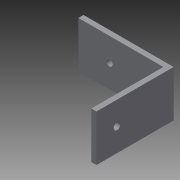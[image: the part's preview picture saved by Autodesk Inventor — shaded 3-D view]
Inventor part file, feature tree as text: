
AUTODESK INVENTOR PART (.ipt)
format: ipt  version: 2015 (Build 190159000, 159)  size: 98,304 bytes
history: native  units: in
note: dims shown in document units (in); Inventor stores cm internally (conversion verified against a paired STEP export)
features: sketch x4, extrude x3, hole x1, projected_geometry x1
ambient origin geometry x8: Origin, YZ Plane, XZ Plane, XY Plane, X Axis, Y Axis, Z Axis, Center Point
bodies: Solid1 (feature_tree)
feature tree (9):
  extrude  "Extrusion1"  Depth=1.75in
  extrude  "Extrusion2"  Depth=0.1in
  hole  "Hole2"  [1 undecoded]
  extrude  "Extrusion3"  Depth=0.05in
  sketch  "Sketch1"  dims[d0=0.9in d1=1.75in]
  sketch  "Sketch2"  dims[d2=0.1in d3=0.0in d4=0.1in]
  sketch  "Sketch4"  dims[d5=1.4in d6=0.0in d16=0.45in]
  projected_geometry  "Projected Loop2"
  sketch  "Sketch5"  dims[d17=1.05in d18=0.128in d19=0.75in d20=0.375in d21=0.25in d22=0.5635in d23=1.0in d24=0.8108in d25=0.05in d26=1.0in d27=0.0in d28=1.0in]
note: 1 required parameter value undecoded (feature->parameter linkage not recoverable at this tier; creation-order binding heuristic only, values carry confidence <= 0.55)
